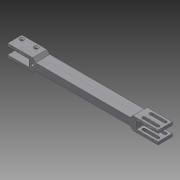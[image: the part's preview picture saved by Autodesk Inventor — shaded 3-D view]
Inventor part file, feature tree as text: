
AUTODESK INVENTOR PART (.ipt)
format: ipt  version: 2015 (Build 190159000, 159)  size: 187,392 bytes
history: native  units: mm
features: sketch x8, extrude x6, chamfer x2, hole x1
ambient origin geometry x8: Origin, YZ Plane, XZ Plane, XY Plane, X Axis, Y Axis, Z Axis, Center Point
bodies: Solid1 (feature_tree)
feature tree (17):
  extrude  "Extrusion1"  Depth=20.0mm
  sketch  "Sketch2"  dims[d2=10.0mm d3=0.0mm d4=4.0mm]
  extrude  "Extrusion2"  Depth=4.0mm
  extrude  "Extrusion3"  Depth=4.0mm TaperAngle=0.0deg
  hole  "Hole1"  [1 undecoded]
  chamfer  "Chamfer1"  Distance=4.0mm Angle=45.0deg
  extrude  "Extrusion4"  Depth=4.0mm
  extrude  "Extrusion5"  Depth=4.0mm
  chamfer  "Chamfer2"  Distance=5.0mm
  extrude  "Extrusion6"  Depth=20.0mm TaperAngle=0.0deg
  sketch  "Sketch1"  dims[d0=150.0mm d1=20.0mm]
  sketch  "Sketch3"  dims[d5=4.0mm d6=5.0mm d7=0.0mm]
  sketch  "Sketch4"  dims[d8=30.0mm d9=0.0mm d10=5.0mm]
  sketch  "Sketch5"  dims[d11=5.0mm]
  sketch  "Sketch6"  dims[d12=5.0mm]
  sketch  "Sketch7"  dims[d13=5.0mm]
  sketch  "Sketch8"  dims[d14=3.0mm d15=6.0mm d16=6.0mm d17=2.0mm d18=90.0deg d19=30.0mm d20=20.594885mm d21=4.0mm d22=2.0mm d23=45.0deg d24=4.0mm d25=4.0mm d26=5.0mm d27=20.0mm d28=0.0mm d29=30.0mm d30=30.0mm d31=4.0mm d32=4.0mm d33=20.0mm d34=0.0mm d35=4.0mm d36=2.0mm d37=45.0deg d38=5.0mm d39=5.0mm d40=5.0mm d41=5.0mm d42=5.0mm d43=5.0mm d44=5.0mm d45=5.0mm d46=4.0mm d47=4.0mm d48=4.0mm d49=4.0mm d50=20.0mm d51=0.0mm]
note: 1 required parameter value undecoded (feature->parameter linkage not recoverable at this tier; creation-order binding heuristic only, values carry confidence <= 0.55)
